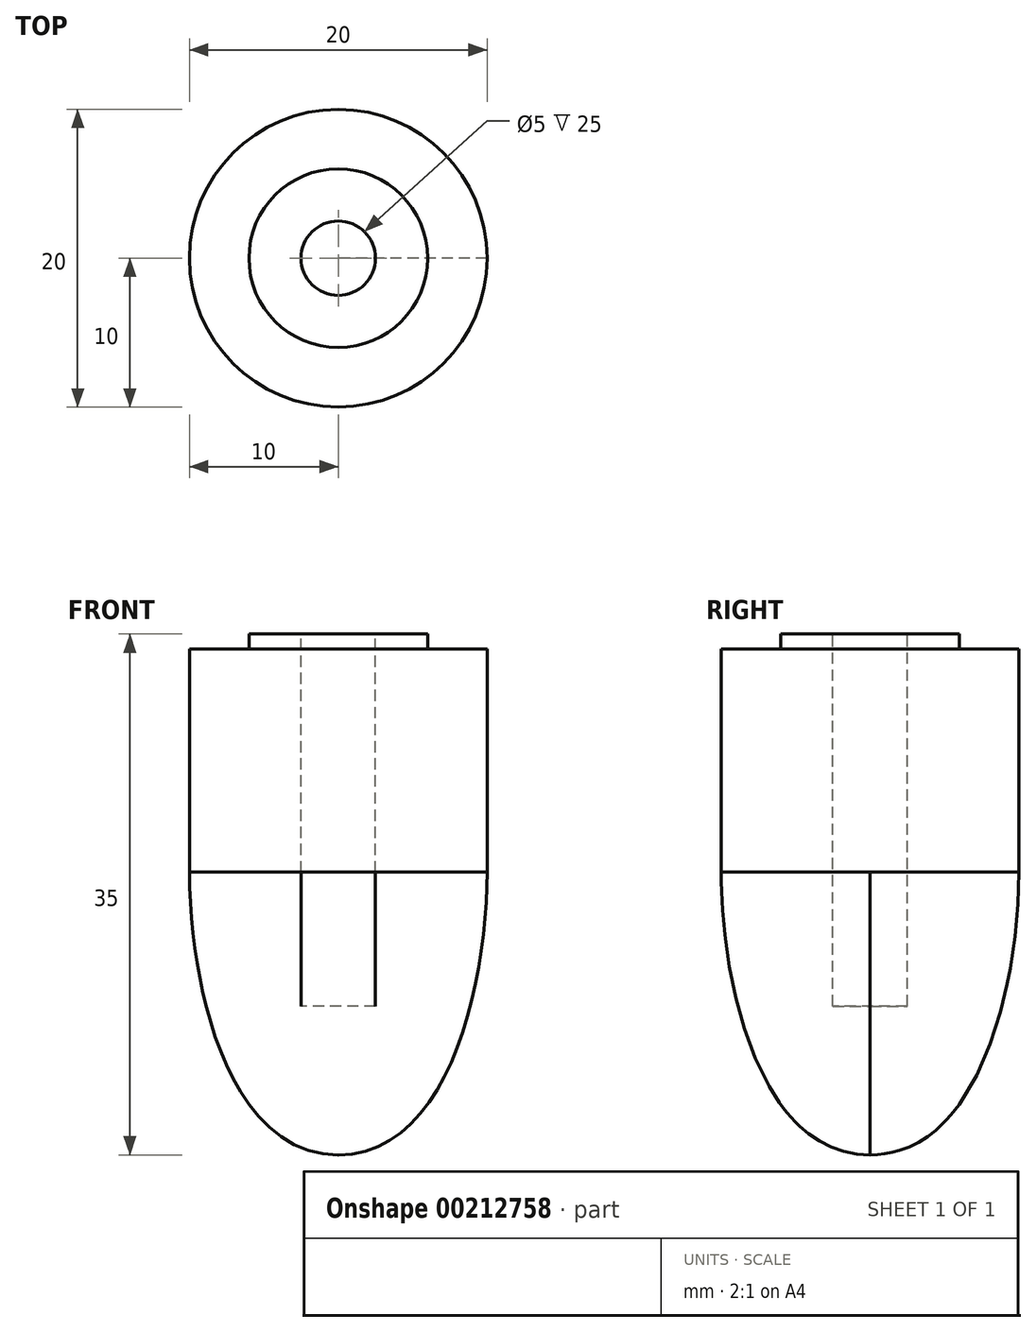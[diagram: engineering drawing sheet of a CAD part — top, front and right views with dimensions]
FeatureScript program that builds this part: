
annotation { "Feature Type Name" : "Feature", "Feature Type Description" : "" }
export const myFeature = defineFeature(function(context is Context, id is Id, definition is map)
    precondition{}
    {
        {
            var Q0;
            Q0=qCreatedBy(makeId("Front.planeOp"),FACE);
            var sketch = newSketch(context, id + "F0", { "sketchPlane" : qUnion([Q0])});
            skLineSegment(sketch, "E0", {"start": v(0, 0) * mm, "end": v(26.5, 0) * mm});
            skLineSegment(sketch, "E1", {"start": v(-7.5, 10) * mm, "end": v(7.5, 10) * mm});
            skFitSpline(sketch, "E2", {"points": [v(7.5, 10) * mm, v(26.5, 0) * mm], "startDerivative": vector(22.36, 0) * mm, "endDerivative": vector(0, -22.36) * mm});
            skLineSegment(sketch, "E3", {"start": v(-8.5, 6) * mm, "end": v(-8.5, 0) * mm});
            skLineSegment(sketch, "E4", {"start": v(0, 0) * mm, "end": v(-8.5, 0) * mm});
            skLineSegment(sketch, "E5", {"start": v(-7.5, 10) * mm, "end": v(-7.5, 6) * mm});
            skLineSegment(sketch, "E6", {"start": v(-7.5, 6) * mm, "end": v(-8.5, 6) * mm});
            skSolve(sketch);
        }
        {
            var Q0;
            Q0=makeQuery(id+"F0.imprint","IMPRINT",FACE,{"disambiguationData":[TD([[makeQuery(id+"F0.imprint","IMPRINT",EDGE,{"derivedFrom":sQuery(id+"F0.wireOp",EDGE,"E0")}),1.0]])]});
            var Q1;
            Q1=sQuery(id+"F0.wireOp",EDGE,"E0");
            revolve(context, id + "F1", {"entities" : qUnion([Q0]), "axis" : qUnion([Q1]), "revolveType" : RevolveType.FULL});
        }
        {
            var Q0;
            Q0=makeQuery(id+"F1.opRevolve","SWEPT_FACE",FACE,{"disambiguationData":[OSD([sQuery(id+"F0.wireOp",EDGE,"E3")])]});
            var sketch = newSketch(context, id + "F2", { "sketchPlane" : qUnion([Q0])});
            skCircle(sketch, "E7", {"center": v(0, 0) * mm, "radius": 2.5 * mm});
            skSolve(sketch);
        }
        {
            var Q0;
            Q0 = qSketchRegion(id + "F2", true);
            extrude(context, id + "F3", {"entities" : qUnion([Q0]), "operationType" : NewBodyOperationType.REMOVE, "oppositeDirection" : true, "depth" : 25 * mm});
        }
        {
            var Q0;
            Q0=qCreatedBy(makeId("Right.planeOp"),FACE);
            var sketch = newSketch(context, id + "F4", { "sketchPlane" : qUnion([Q0])});
            skLineSegment(sketch, "E8", {"start": v(0, 0) * mm, "end": v(0, 0) * mm});
            skLineSegment(sketch, "E9", {"start": v(0, 0) * mm, "end": v(25.07, 0) * mm});
            skSolve(sketch);
        }
        {
            var Q0;
            Q0=makeQuery(id+"F1.opRevolve","SWEPT_BODY",BODY,{"disambiguationData":[OSD([sQuery(id+"F0.wireOp",EDGE,"E0"),sQuery(id+"F0.wireOp",EDGE,"E1"),sQuery(id+"F0.wireOp",EDGE,"E2"),sQuery(id+"F0.wireOp",EDGE,"E3"),sQuery(id+"F0.wireOp",EDGE,"E4"),sQuery(id+"F0.wireOp",EDGE,"E5"),sQuery(id+"F0.wireOp",EDGE,"E6")])]});
            var Q1;
            Q1=sQuery(id+"F4.wireOp",EDGE,"E8");
            var Q2;
            Q2=sQuery(id+"F4.wireOp",EDGE,"E9");
            transform(context, id + "F5", {"entities" : qUnion([Q0]), "transformType" : TransformType.ROTATION, "transformAxis" : qUnion([Q2]), "angle" : 90 * degree, "makeCopy" : false});
        }
    });
